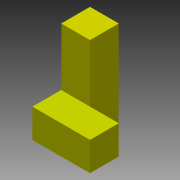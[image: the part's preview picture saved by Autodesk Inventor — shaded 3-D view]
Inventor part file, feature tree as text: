
AUTODESK INVENTOR PART (.ipt)
format: ipt  version: 2015 (Build 190159000, 159)  size: 97,280 bytes
history: native  units: in
note: dims shown in document units (in); Inventor stores cm internally (conversion verified against a paired STEP export)
features: extrude x2, sketch x2
ambient origin geometry x8: Origin, YZ Plane, XZ Plane, XY Plane, X Axis, Y Axis, Z Axis, Center Point
bodies: Solid1 (feature_tree)
feature tree (4):
  extrude  "Extrusion1"  Depth=0.75in
  extrude  "Extrusion2"  Depth=1.5in
  sketch  "Sketch1"  dims[d0=2.25in d1=0.75in]
  sketch  "Sketch2"  dims[d2=0.75in d3=0.0in d4=1.5in d5=0.75in d6=0.75in d7=0.0in]
